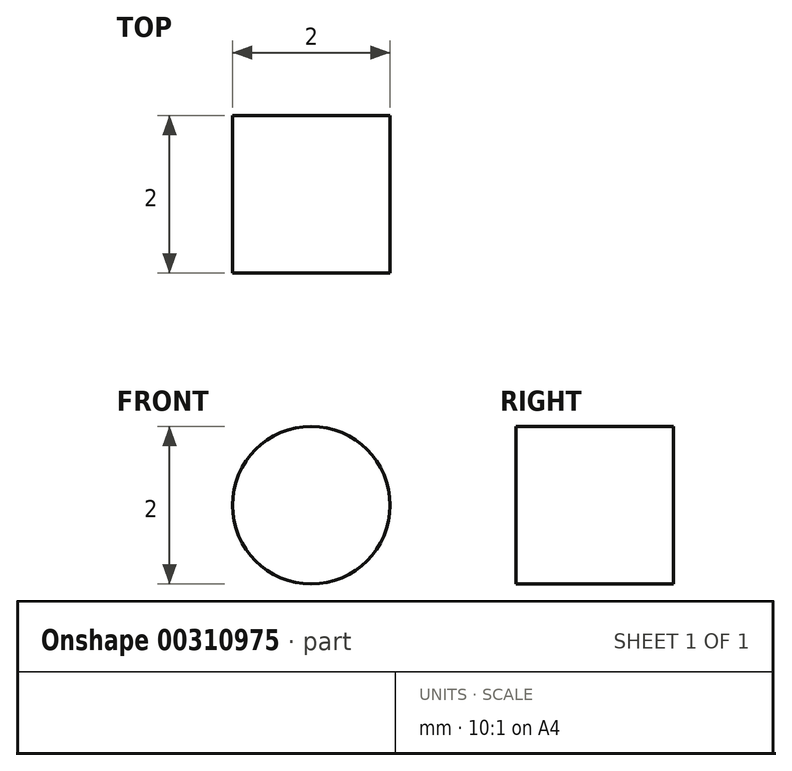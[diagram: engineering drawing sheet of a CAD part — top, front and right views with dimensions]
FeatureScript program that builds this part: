
annotation { "Feature Type Name" : "Feature", "Feature Type Description" : "" }
export const myFeature = defineFeature(function(context is Context, id is Id, definition is map)
    precondition{}
    {
        {
            var Q0;
            Q0=qCreatedBy(makeId("Front.planeOp"),FACE);
            var sketch = newSketch(context, id + "F0", { "sketchPlane" : qUnion([Q0])});
            skCircle(sketch, "E0", {"center": v(0, 0) * mm, "radius": 1 * mm});
            skSolve(sketch);
        }
        {
            var Q0;
            Q0=makeQuery(id+"F0.imprint","IMPRINT",FACE,{"disambiguationData":[TD([[makeQuery(id+"F0.imprint","IMPRINT",EDGE,{"derivedFrom":sQuery(id+"F0.wireOp",EDGE,"E0")}),1.0]])]});
            extrude(context, id + "F1", {"entities" : qUnion([Q0]), "depth" : 2 * mm});
        }
    });
